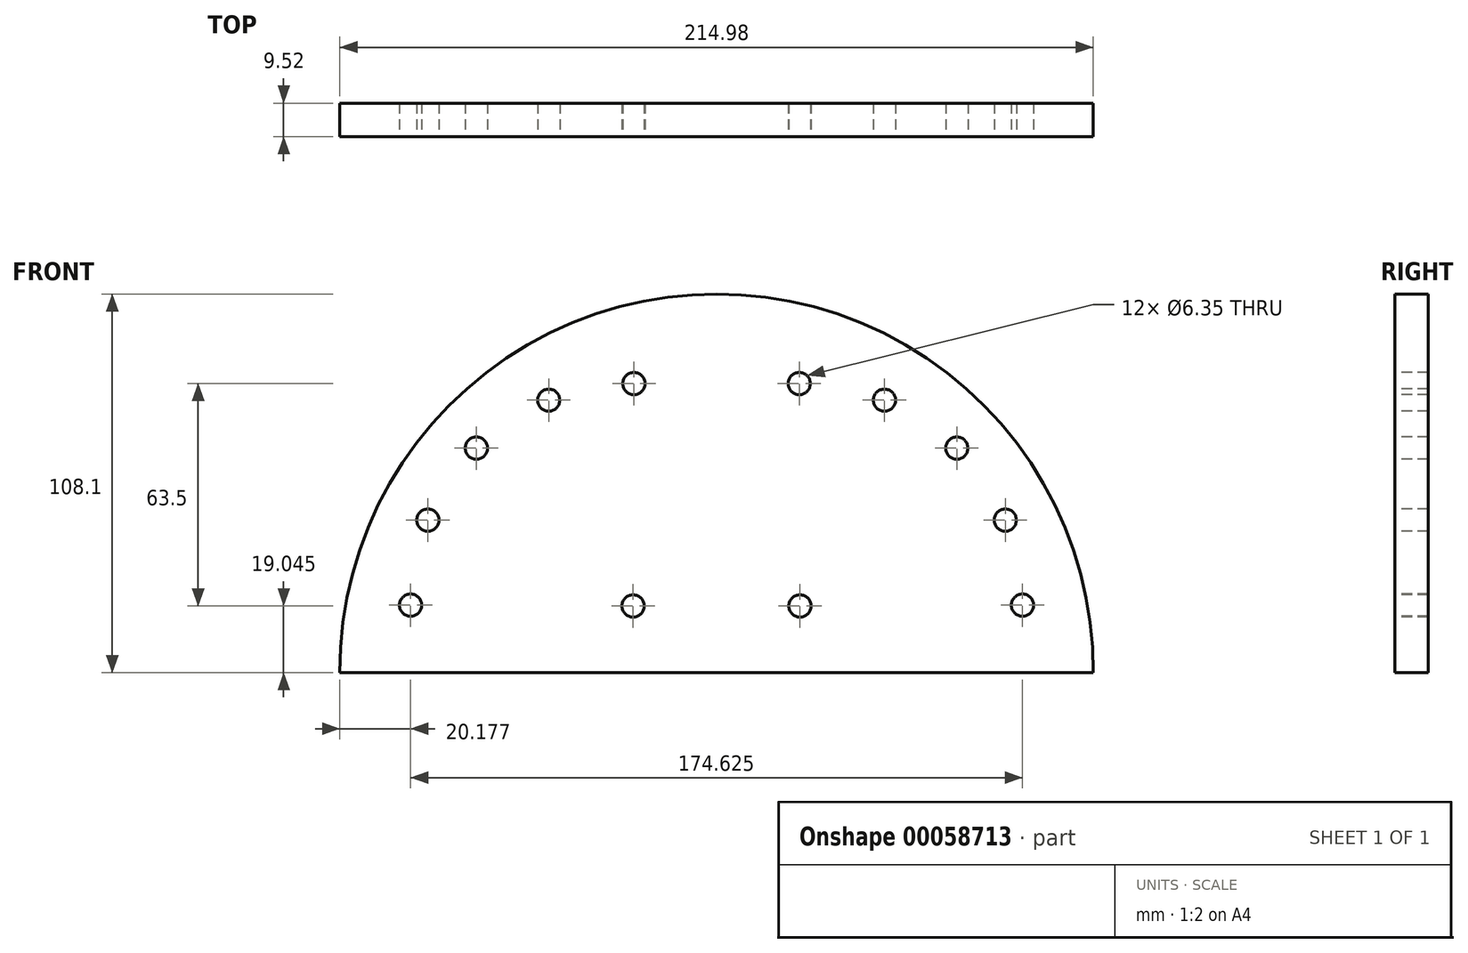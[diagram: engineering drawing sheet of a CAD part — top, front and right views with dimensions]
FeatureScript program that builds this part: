
annotation { "Feature Type Name" : "Feature", "Feature Type Description" : "" }
export const myFeature = defineFeature(function(context is Context, id is Id, definition is map)
    precondition{}
    {
        {
            var Q0;
            Q0=qCreatedBy(makeId("Front.planeOp"),FACE);
            var sketch = newSketch(context, id + "F0", { "sketchPlane" : qUnion([Q0])});
            skLineSegment(sketch, "E0", {"start": v(-107.5, -0.61) * mm, "end": v(108.4, -0.61) * mm});
            skArc(sketch, "E1", {"start": v(-107.5, -0.61) * mm, "mid": v(0, 107.5) * mm, "end": v(107.5, -0.61) * mm});
            skSolve(sketch);
        }
        {
            var Q0;
            Q0=qSketchRegion(id+"F0",true);
            extrude(context, id + "F1", {"entities" : qUnion([Q0]), "endBound" : BoundingType.SYMMETRIC, "depth" : 9.52 * mm});
        }
        {
            var Q0;
            Q0=makeQuery(id+"F1.opExtrude","CAP_FACE",FACE,{"disambiguationData":[OSD([sQuery(id+"F0.wireOp",EDGE,"E0"),sQuery(id+"F0.wireOp",EDGE,"E1")])],"isStart":false});
            var sketch = newSketch(context, id + "F2", { "sketchPlane" : qUnion([Q0])});
            skCircle(sketch, "E2", {"center": v(23.81, 18.44) * mm, "radius": 3.18 * mm});
            skCircle(sketch, "E3", {"center": v(23.59, 81.94) * mm, "radius": 3.18 * mm});
            skCircle(sketch, "E4.1.0", {"center": v(47.9, 77.19) * mm, "radius": 3.18 * mm});
            skCircle(sketch, "E4.2.0", {"center": v(68.55, 63.5) * mm, "radius": 3.18 * mm});
            skLineSegment(sketch, "E4.anchor1", {"start": v(0, 18.44) * mm, "end": v(0, 94.64) * mm, "construction": true});
            skLineSegment(sketch, "E4.anchor2", {"start": v(-4.4, 18.66) * mm, "end": v(87.31, 18.66) * mm, "construction": true});
            skCircle(sketch, "E5.1.3.0", {"center": v(82.4, 42.94) * mm, "radius": 3.18 * mm});
            skCircle(sketch, "E5.1.4.0", {"center": v(87.31, 18.66) * mm, "radius": 3.18 * mm});
            skCircle(sketch, "E6.MirrorC", {"center": v(-23.59, 81.94) * mm, "radius": 3.18 * mm});
            skCircle(sketch, "E7.MirrorC", {"center": v(-47.9, 77.19) * mm, "radius": 3.18 * mm});
            skCircle(sketch, "E8.MirrorC", {"center": v(-68.55, 63.5) * mm, "radius": 3.18 * mm});
            skCircle(sketch, "E9.MirrorC", {"center": v(-82.4, 42.94) * mm, "radius": 3.18 * mm});
            skCircle(sketch, "E10.MirrorC", {"center": v(-87.31, 18.66) * mm, "radius": 3.18 * mm});
            skCircle(sketch, "E11.MirrorC", {"center": v(-23.81, 18.44) * mm, "radius": 3.18 * mm});
            skSolve(sketch);
        }
        {
            var Q0;
            Q0=sQuery(id+"F2.wireOp",VERTEX,"E2.center");
            var Q1;
            Q1=sQuery(id+"F2.wireOp",VERTEX,"E4.anchor2.end");
            var Q2;
            Q2=sQuery(id+"F2.wireOp",VERTEX,"E4.1.0.center");
            var Q3;
            Q3=sQuery(id+"F2.wireOp",VERTEX,"E3.center");
            var Q4;
            Q4=sQuery(id+"F2.wireOp",VERTEX,"E4.2.0.center");
            var Q5;
            Q5=sQuery(id+"F2.wireOp",VERTEX,"E5.1.3.0.center");
            var Q6;
            Q6=sQuery(id+"F2.wireOp",VERTEX,"E11.MirrorC.center");
            var Q7;
            Q7=sQuery(id+"F2.wireOp",VERTEX,"E6.MirrorC.center");
            var Q8;
            Q8=sQuery(id+"F2.wireOp",VERTEX,"E7.MirrorC.center");
            var Q9;
            Q9=sQuery(id+"F2.wireOp",VERTEX,"E8.MirrorC.center");
            var Q10;
            Q10=sQuery(id+"F2.wireOp",VERTEX,"E9.MirrorC.center");
            var Q11;
            Q11=sQuery(id+"F2.wireOp",VERTEX,"E10.MirrorC.center");
            var Q12;
            Q12=makeQuery(id+"F1.opExtrude","SWEPT_BODY",BODY,{"disambiguationData":[OSD([sQuery(id+"F0.wireOp",EDGE,"E0"),sQuery(id+"F0.wireOp",EDGE,"E1")])]});
            hole(context, id + "F3", {"style" : HoleStyle.SIMPLE, "holeDiameter" : 6.35 * mm, "endStyle" : HoleEndStyle.THROUGH, "locations" : qUnion([Q0, Q1, Q2, Q3, Q4, Q5, Q6, Q7, Q8, Q9, Q10, Q11]), "scope" : qUnion([Q12])});
        }
    });
